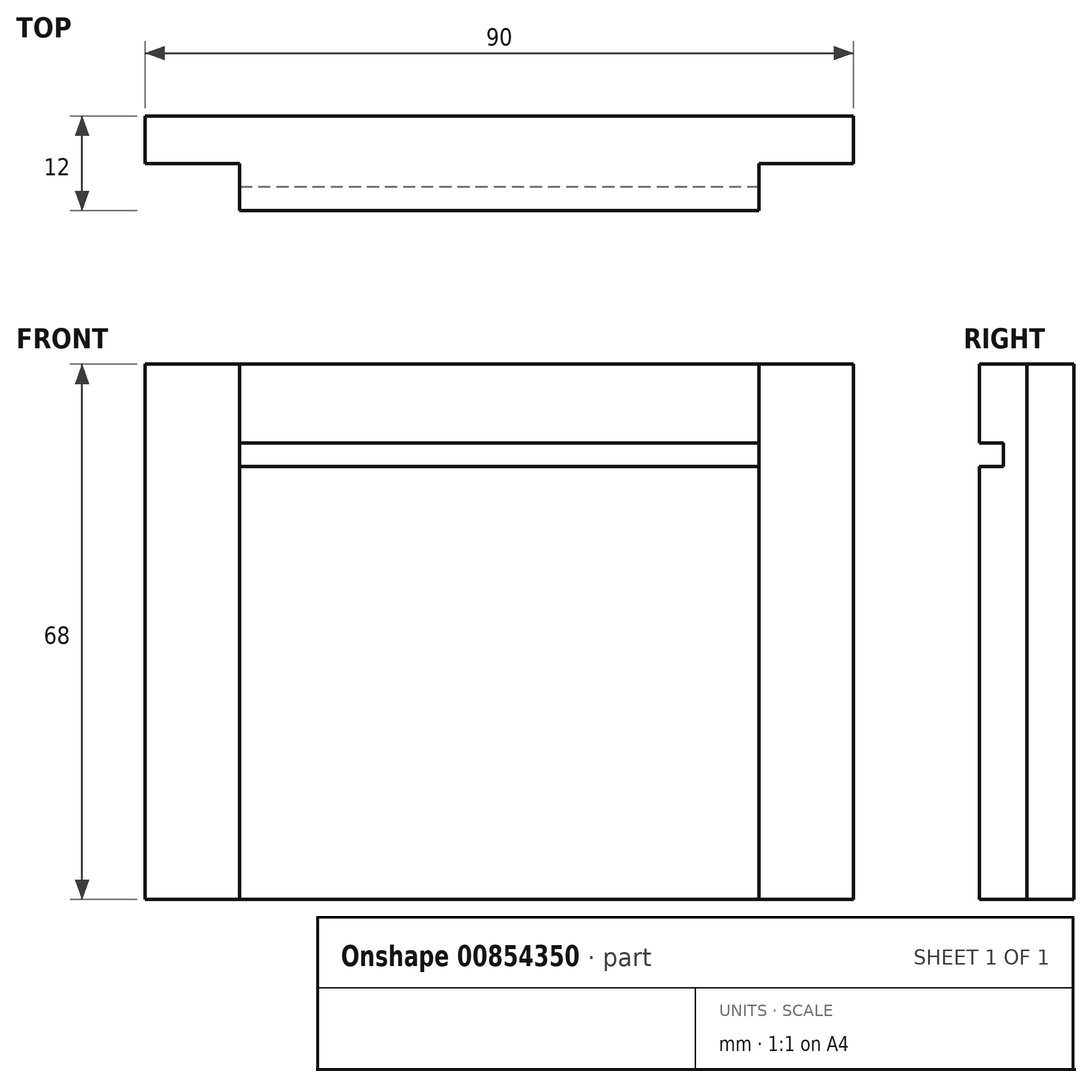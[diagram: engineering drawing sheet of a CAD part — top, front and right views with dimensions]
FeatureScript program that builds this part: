
annotation { "Feature Type Name" : "Feature", "Feature Type Description" : "" }
export const myFeature = defineFeature(function(context is Context, id is Id, definition is map)
    precondition{}
    {
        {
            var Q0;
            Q0=qCreatedBy(makeId("Front.planeOp"),FACE);
            var sketch = newSketch(context, id + "F0", { "sketchPlane" : qUnion([Q0])});
            skLineSegment(sketch, "E0.bottom", {"start": v(-20, 34) * mm, "end": v(20, 34) * mm});
            skLineSegment(sketch, "E0.top", {"start": v(-20, -34) * mm, "end": v(20, -34) * mm});
            skLineSegment(sketch, "E0.left", {"start": v(-20, 34) * mm, "end": v(-20, -34) * mm});
            skLineSegment(sketch, "E0.right", {"start": v(20, 34) * mm, "end": v(20, -34) * mm});
            skPoint(sketch, "E0.middle", {"position": v(0, 0) * mm});
            skSolve(sketch);
        }
        {
            var Q0;
            Q0 = qSketchRegion(id + "F0", true);
            extrude(context, id + "F1", {"entities" : qUnion([Q0]), "depth" : 12 * mm, "offsetDistance" : 25.4 * mm});
        }
        {
            var Q0;
            Q0=makeQuery(id+"F1.opExtrude","SWEPT_FACE",FACE,{"disambiguationData":[OSD([sQuery(id+"F0.wireOp",EDGE,"E0.right")])]});
            var sketch = newSketch(context, id + "F2", { "sketchPlane" : qUnion([Q0])});
            skLineSegment(sketch, "E1.bottom", {"start": v(-12, 21) * mm, "end": v(-7, 21) * mm});
            skLineSegment(sketch, "E1.top", {"start": v(-12, 24) * mm, "end": v(-7, 24) * mm});
            skLineSegment(sketch, "E1.left", {"start": v(-12, 21) * mm, "end": v(-12, 24) * mm});
            skLineSegment(sketch, "E1.right", {"start": v(-7, 21) * mm, "end": v(-7, 24) * mm});
            skSolve(sketch);
        }
        {
            var Q0;
            Q0 = qSketchRegion(id + "F2", true);
            extrude(context, id + "F3", {"entities" : qUnion([Q0]), "operationType" : NewBodyOperationType.REMOVE, "oppositeDirection" : true, "depth" : 59 * mm, "offsetDistance" : 25.4 * mm});
        }
        {
            var Q0;
            Q0=makeQuery(id+"F1.opExtrude","SWEPT_BODY",BODY,{"disambiguationData":[OSD([sQuery(id+"F0.wireOp",EDGE,"E0.bottom"),sQuery(id+"F0.wireOp",EDGE,"E0.top"),sQuery(id+"F0.wireOp",EDGE,"E0.left"),sQuery(id+"F0.wireOp",EDGE,"E0.right")])]});
            deleteBodies(context, id + "F4", {"entities" : qUnion([Q0])});
        }
        {
            var Q0;
            Q0=qCreatedBy(makeId("Front.planeOp"),FACE);
            var sketch = newSketch(context, id + "F5", { "sketchPlane" : qUnion([Q0])});
            skLineSegment(sketch, "E2.bottom", {"start": v(-45, 34) * mm, "end": v(45, 34) * mm});
            skLineSegment(sketch, "E2.top", {"start": v(-45, -34) * mm, "end": v(45, -34) * mm});
            skLineSegment(sketch, "E2.left", {"start": v(-45, 34) * mm, "end": v(-45, -34) * mm});
            skLineSegment(sketch, "E2.right", {"start": v(45, 34) * mm, "end": v(45, -34) * mm});
            skPoint(sketch, "E2.middle", {"position": v(0, 0) * mm});
            skSolve(sketch);
        }
        {
            var Q0;
            Q0 = qSketchRegion(id + "F5", true);
            extrude(context, id + "F6", {"entities" : qUnion([Q0]), "depth" : 12 * mm, "offsetDistance" : 25.4 * mm});
        }
        {
            var Q0;
            Q0=makeQuery(id+"F6.opExtrude","SWEPT_FACE",FACE,{"disambiguationData":[OSD([sQuery(id+"F5.wireOp",EDGE,"E2.left")])]});
            var sketch = newSketch(context, id + "F7", { "sketchPlane" : qUnion([Q0])});
            skLineSegment(sketch, "E3.bottom", {"start": v(12, 24) * mm, "end": v(9, 24) * mm});
            skLineSegment(sketch, "E3.top", {"start": v(12, 21) * mm, "end": v(9, 21) * mm});
            skLineSegment(sketch, "E3.left", {"start": v(12, 24) * mm, "end": v(12, 21) * mm});
            skLineSegment(sketch, "E3.right", {"start": v(9, 24) * mm, "end": v(9, 21) * mm});
            skSolve(sketch);
        }
        {
            var Q0;
            Q0 = qSketchRegion(id + "F7", true);
            extrude(context, id + "F8", {"entities" : qUnion([Q0]), "operationType" : NewBodyOperationType.REMOVE, "oppositeDirection" : true, "depth" : 200 * mm, "offsetDistance" : 25.4 * mm});
        }
        {
            var Q0;
            {var subQ0=sQuery(id+"F5.wireOp",EDGE,"E2.top");var subQ1=sQuery(id+"F5.wireOp",EDGE,"E2.left");var subQ2=sQuery(id+"F5.wireOp",EDGE,"E2.right");Q0=makeQuery(id+"F8.boolean.opBoolean","SPLIT",FACE,{"disambiguationData":[TD([makeQuery(id+"F6.opExtrude","SWEPT_FACE",FACE,{"disambiguationData":[OSD([subQ0])]})])],"derivedFrom":makeQuery(id+"F6.opExtrude","CAP_FACE",FACE,{"disambiguationData":[OSD([sQuery(id+"F5.wireOp",EDGE,"E2.bottom"),subQ0,subQ1,subQ2])],"isStart":false})});}
            var sketch = newSketch(context, id + "F9", { "sketchPlane" : qUnion([Q0])});
            skLineSegment(sketch, "E4.bottom", {"start": v(-45, 34.27) * mm, "end": v(-33, 34.27) * mm});
            skLineSegment(sketch, "E4.top", {"start": v(-45, -34) * mm, "end": v(-33, -34) * mm});
            skLineSegment(sketch, "E4.left", {"start": v(-45, 34.27) * mm, "end": v(-45, -34) * mm});
            skLineSegment(sketch, "E4.right", {"start": v(-33, 34.27) * mm, "end": v(-33, -34) * mm});
            skLineSegment(sketch, "E5.bottom", {"start": v(45, 34.71) * mm, "end": v(33, 34.71) * mm});
            skLineSegment(sketch, "E5.top", {"start": v(45, -34) * mm, "end": v(33, -34) * mm});
            skLineSegment(sketch, "E5.left", {"start": v(45, 34.71) * mm, "end": v(45, -34) * mm});
            skLineSegment(sketch, "E5.right", {"start": v(33, 34.71) * mm, "end": v(33, -34) * mm});
            skSolve(sketch);
        }
        {
            var Q0;
            Q0 = qSketchRegion(id + "F9", true);
            extrude(context, id + "F10", {"entities" : qUnion([Q0]), "operationType" : NewBodyOperationType.REMOVE, "oppositeDirection" : true, "depth" : 6 * mm, "offsetDistance" : 25.4 * mm});
        }
    });
